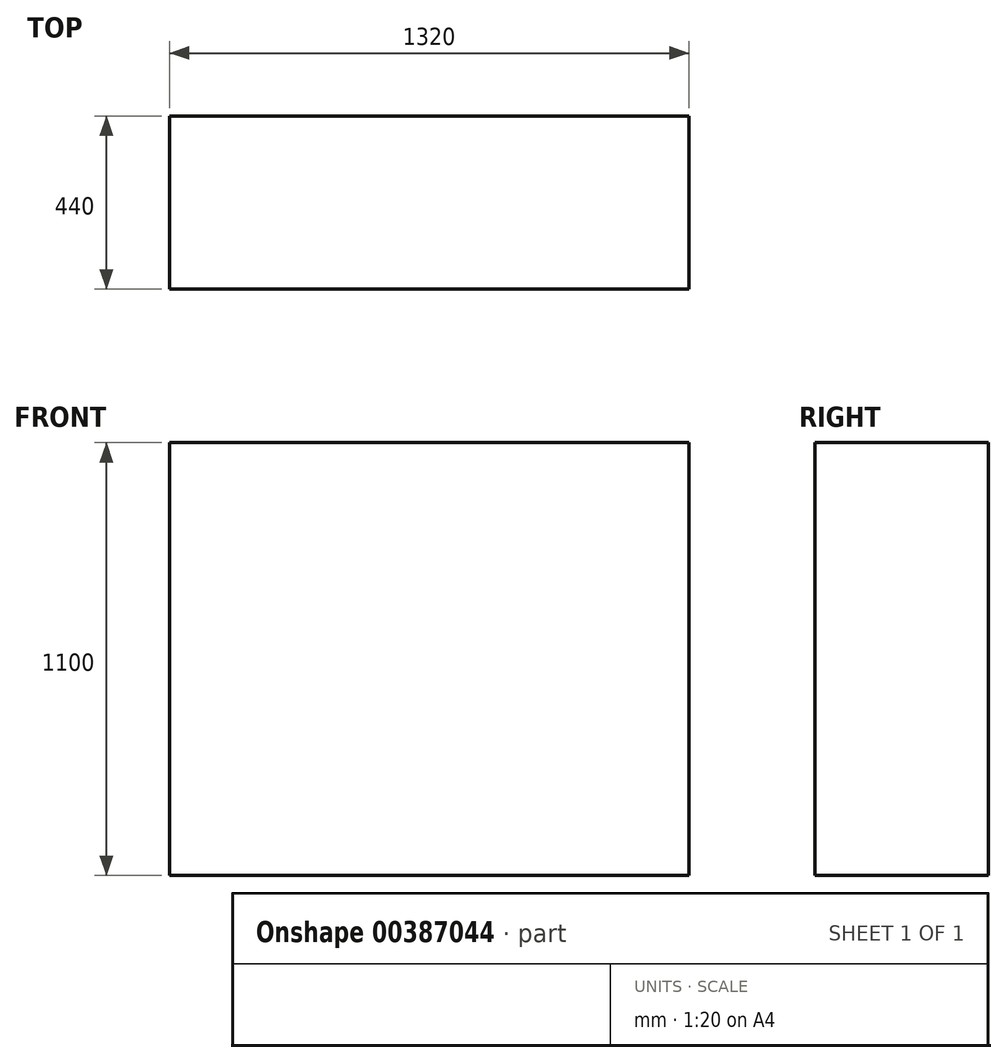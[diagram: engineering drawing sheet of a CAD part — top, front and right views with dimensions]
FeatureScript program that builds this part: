
annotation { "Feature Type Name" : "Feature", "Feature Type Description" : "" }
export const myFeature = defineFeature(function(context is Context, id is Id, definition is map)
    precondition{}
    {
        {
            var Q0;
            Q0=qCreatedBy(makeId("Top.planeOp"),FACE);
            var sketch = newSketch(context, id + "F0", { "sketchPlane" : qUnion([Q0])});
            skLineSegment(sketch, "E0.bottom", {"start": v(0, 0) * mm, "end": v(1320, 0) * mm});
            skLineSegment(sketch, "E0.top", {"start": v(0, 440) * mm, "end": v(1320, 440) * mm});
            skLineSegment(sketch, "E0.left", {"start": v(0, 0) * mm, "end": v(0, 440) * mm});
            skLineSegment(sketch, "E0.right", {"start": v(1320, 0) * mm, "end": v(1320, 440) * mm});
            skSolve(sketch);
        }
        {
            var Q0;
            Q0=qSketchRegion(id+"F0",true);
            extrude(context, id + "F1", {"entities" : qUnion([Q0]), "depth" : 1100 * mm});
        }
    });
